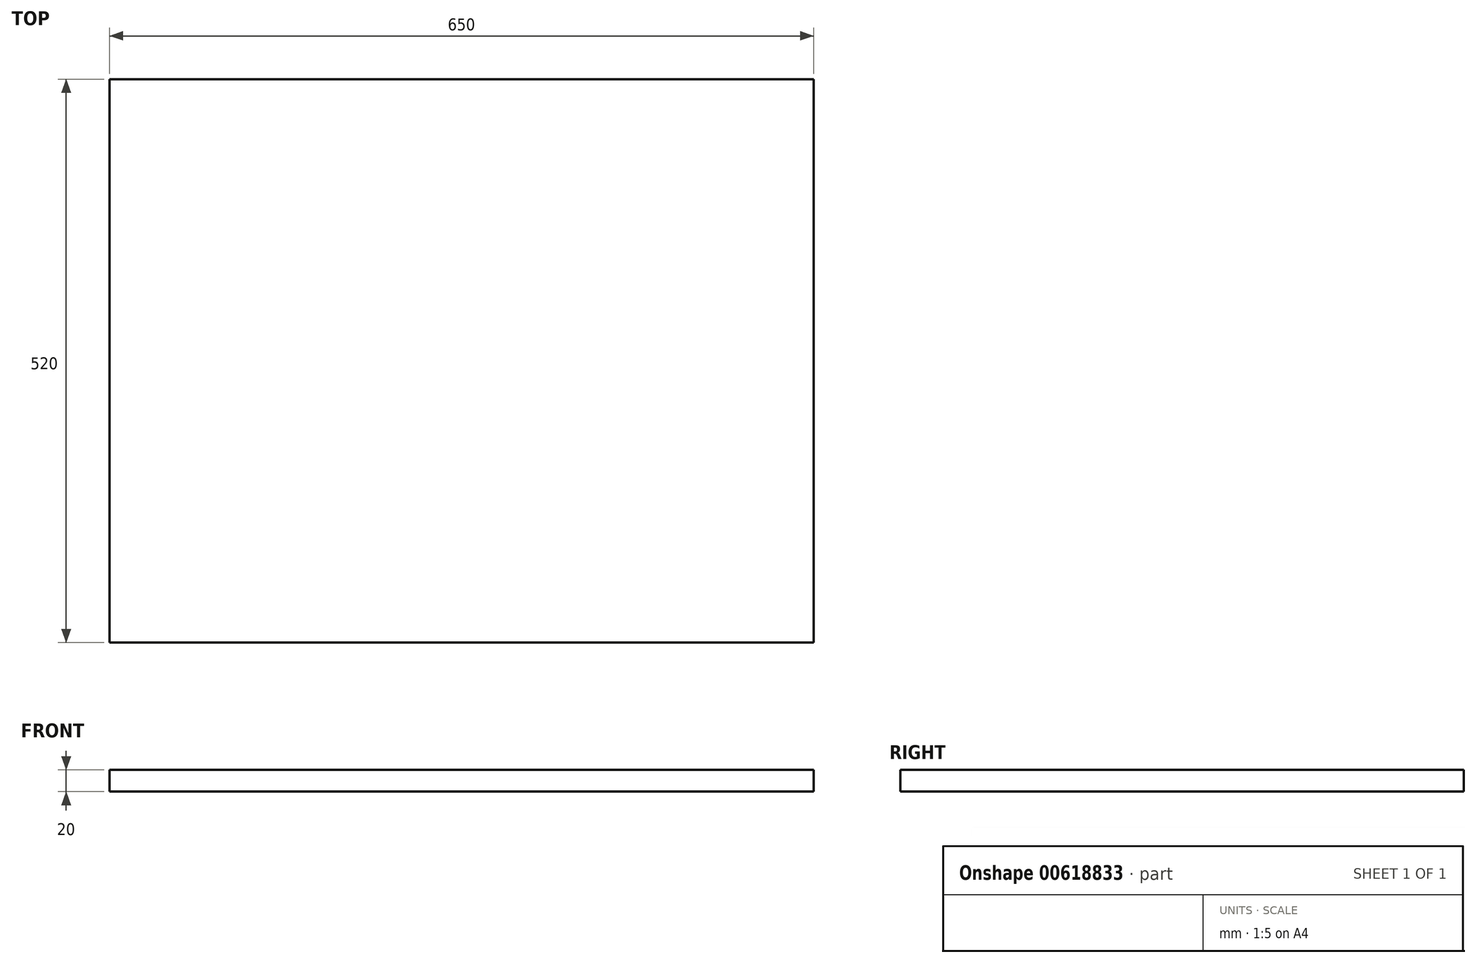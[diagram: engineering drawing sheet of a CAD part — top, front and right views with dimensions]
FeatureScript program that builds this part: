
annotation { "Feature Type Name" : "Feature", "Feature Type Description" : "" }
export const myFeature = defineFeature(function(context is Context, id is Id, definition is map)
    precondition{}
    {
        {
            var Q0;
            Q0=qCreatedBy(makeId("Top.planeOp"),FACE);
            var sketch = newSketch(context, id + "F0", { "sketchPlane" : qUnion([Q0])});
            skLineSegment(sketch, "E0.bottom", {"start": v(-325, 260) * mm, "end": v(325, 260) * mm});
            skLineSegment(sketch, "E0.top", {"start": v(-325, -260) * mm, "end": v(325, -260) * mm});
            skLineSegment(sketch, "E0.left", {"start": v(-325, 260) * mm, "end": v(-325, -260) * mm});
            skLineSegment(sketch, "E0.right", {"start": v(325, 260) * mm, "end": v(325, -260) * mm});
            skPoint(sketch, "E0.middle", {"position": v(0, 0) * mm});
            skSolve(sketch);
        }
        {
            var Q0;
            Q0 = qSketchRegion(id + "F0", true);
            extrude(context, id + "F1", {"entities" : qUnion([Q0]), "depth" : 20 * mm, "offsetDistance" : 25 * mm});
        }
    });
